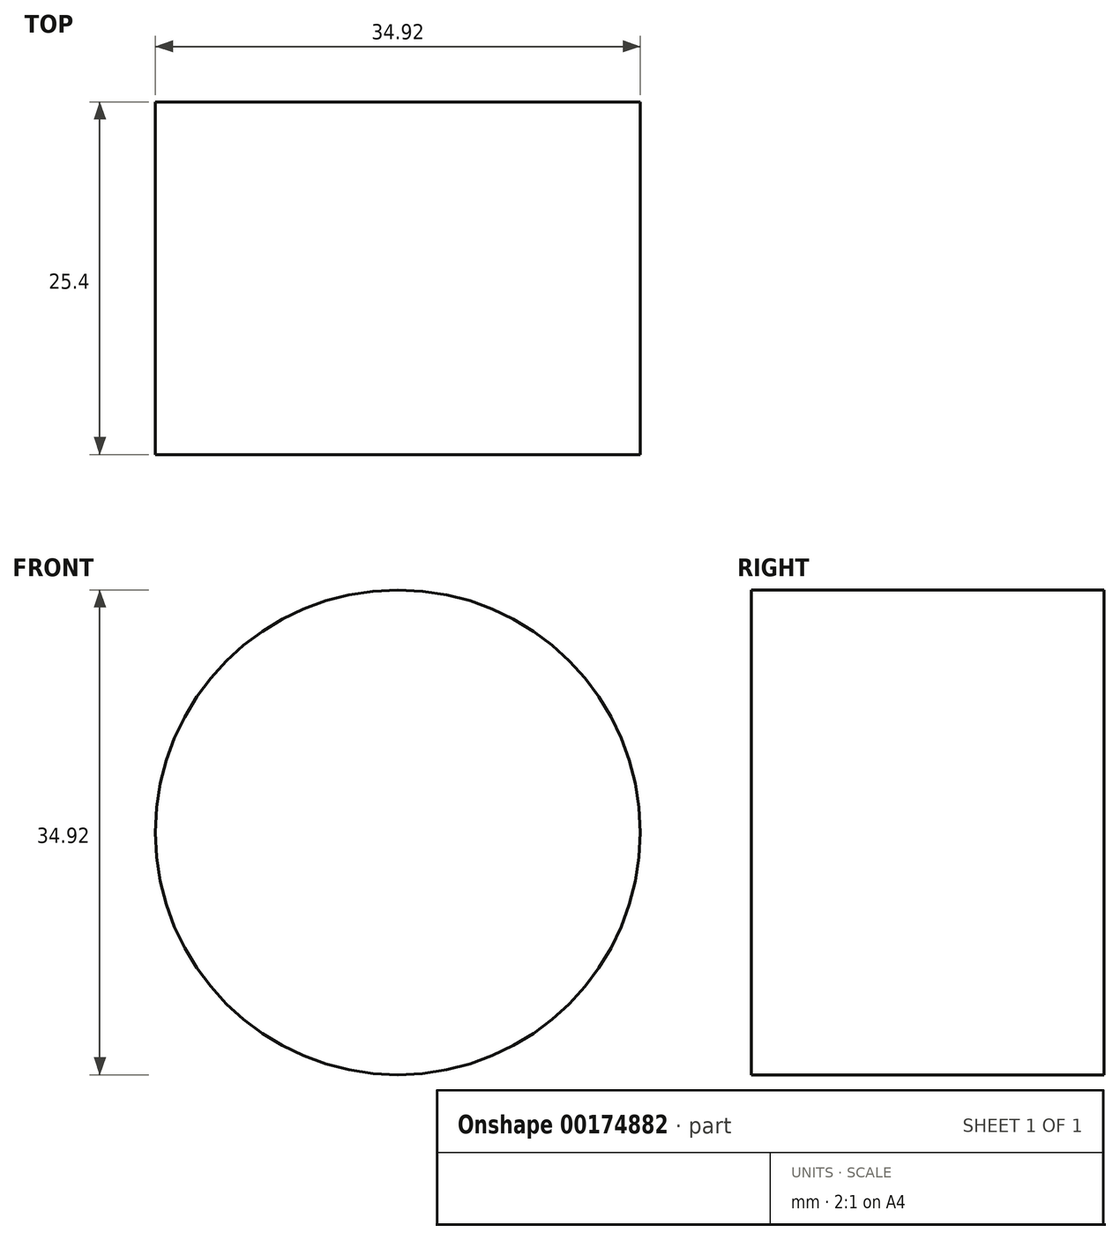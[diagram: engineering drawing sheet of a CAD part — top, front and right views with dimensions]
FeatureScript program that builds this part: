
annotation { "Feature Type Name" : "Feature", "Feature Type Description" : "" }
export const myFeature = defineFeature(function(context is Context, id is Id, definition is map)
    precondition{}
    {
        {
            var Q0;
            Q0=qCreatedBy(makeId("Front.planeOp"),FACE);
            var sketch = newSketch(context, id + "F0", { "sketchPlane" : qUnion([Q0])});
            skCircle(sketch, "E0", {"center": v(0, 0) * mm, "radius": 17.46 * mm});
            skSolve(sketch);
        }
        {
            var Q0;
            Q0 = qSketchRegion(id + "F0", true);
            extrude(context, id + "F1", {"entities" : qUnion([Q0]), "depth" : 25.4 * mm});
        }
    });
